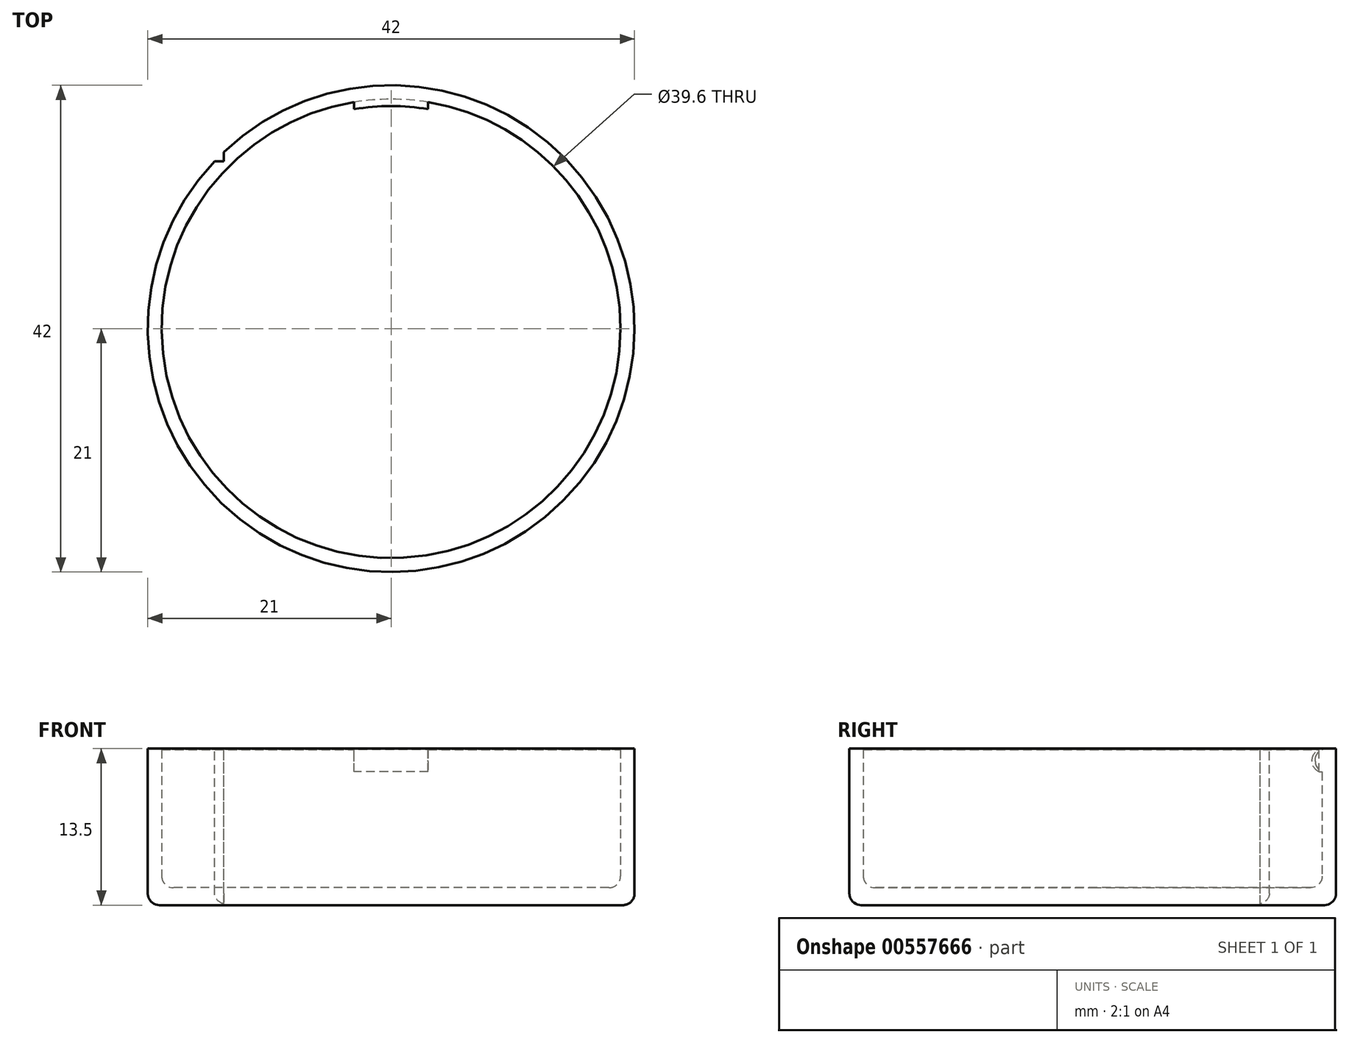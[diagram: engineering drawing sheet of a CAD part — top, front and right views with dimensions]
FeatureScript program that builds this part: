
annotation { "Feature Type Name" : "Feature", "Feature Type Description" : "" }
export const myFeature = defineFeature(function(context is Context, id is Id, definition is map)
    precondition{}
    {
        {
            var Q0;
            Q0=qCreatedBy(makeId("Top.planeOp"),FACE);
            var sketch = newSketch(context, id + "F0", { "sketchPlane" : qUnion([Q0])});
            skCircle(sketch, "E0", {"center": v(0, 0) * mm, "radius": 21 * mm});
            skSolve(sketch);
        }
        {
            var Q0;
            Q0=makeQuery(id+"F0.imprint","IMPRINT",FACE,{"disambiguationData":[TD([[makeQuery(id+"F0.imprint","IMPRINT",EDGE,{"derivedFrom":sQuery(id+"F0.wireOp",EDGE,"E0")}),1.0]])]});
            extrude(context, id + "F1", {"entities" : qUnion([Q0]), "depth" : 1.5 * mm, "offsetDistance" : 25 * mm});
        }
        {
            var Q0;
            Q0=makeQuery(id+"F1.opExtrude","CAP_FACE",FACE,{"disambiguationData":[OSD([sQuery(id+"F0.wireOp",EDGE,"E0")])],"isStart":false});
            var sketch = newSketch(context, id + "F2", { "sketchPlane" : qUnion([Q0])});
            skCircle(sketch, "E1", {"center": v(0, 0) * mm, "radius": 19.8 * mm});
            skCircle(sketch, "E2", {"center": v(0, 0) * mm, "radius": 21 * mm});
            skSolve(sketch);
        }
        {
            var Q0;
            Q0=makeQuery(id+"F2.imprint","IMPRINT",FACE,{"disambiguationData":[TD([[makeQuery(id+"F2.imprint","IMPRINT",EDGE,{"derivedFrom":sQuery(id+"F2.wireOp",EDGE,"E1")}),-1.0]])]});
            extrude(context, id + "F3", {"entities" : qUnion([Q0]), "operationType" : NewBodyOperationType.ADD, "depth" : 12 * mm, "offsetDistance" : 25 * mm});
        }
        {
            var Q0;
            Q0=makeQuery(id+"F1.opExtrude","CAP_EDGE",EDGE,{"disambiguationData":[OSD([sQuery(id+"F0.wireOp",EDGE,"E0")])],"isStart":true});
            fillet(context, id + "F4", {"entities" : qUnion([Q0]), "radius" : 1 * mm, "tangentPropagation" : true, "allowEdgeOverflow" : false});
        }
        {
            var Q0;
            Q0=makeQuery(id+"F3.opExtrude","CAP_FACE",FACE,{"disambiguationData":[OSD([sQuery(id+"F2.wireOp",EDGE,"E1"),sQuery(id+"F2.wireOp",EDGE,"E2")])],"isStart":false});
            var sketch = newSketch(context, id + "F5", { "sketchPlane" : qUnion([Q0])});
            skLineSegment(sketch, "E3", {"start": v(-15.24, 14.44) * mm, "end": v(-14.44, 14.44) * mm});
            skLineSegment(sketch, "E4", {"start": v(-14.44, 14.44) * mm, "end": v(-14.44, 15.24) * mm});
            skArc(sketch, "E5", {"start": v(-14.44, 15.24) * mm, "mid": v(-14.85, 14.85) * mm, "end": v(-15.24, 14.44) * mm});
            skSolve(sketch);
        }
        {
            var Q0;
            Q0=makeQuery(id+"F5.imprint","IMPRINT",FACE,{"disambiguationData":[TD([[makeQuery(id+"F5.imprint","IMPRINT",EDGE,{"derivedFrom":sQuery(id+"F5.wireOp",EDGE,"E3")}),1.0]])]});
            extrude(context, id + "F6", {"entities" : qUnion([Q0]), "operationType" : NewBodyOperationType.REMOVE, "oppositeDirection" : true, "depth" : 25 * mm, "offsetDistance" : 25 * mm});
        }
        {
            var Q0;
            Q0=makeQuery(id+"F1.opExtrude","CAP_FACE",FACE,{"disambiguationData":[OSD([sQuery(id+"F0.wireOp",EDGE,"E0")])],"isStart":false});
            var Q1;
            Q1=makeQuery(id+"F6.boolean.opBoolean","COPY",EDGE,{"derivedFrom":makeQuery(id+"F6.opExtrude","SWEPT_EDGE",EDGE,{"disambiguationData":[OSD([sQuery(id+"F2.wireOp",EDGE,"E2"),sQuery(id+"F5.wireOp",EDGE,"E4"),sQuery(id+"F5.wireOp",EDGE,"E5")])]})});
            var Q2;
            Q2=makeQuery(id+"F6.boolean.opBoolean","COPY",EDGE,{"derivedFrom":makeQuery(id+"F6.opExtrude","SWEPT_EDGE",EDGE,{"disambiguationData":[OSD([sQuery(id+"F2.wireOp",EDGE,"E2"),sQuery(id+"F5.wireOp",EDGE,"E3"),sQuery(id+"F5.wireOp",EDGE,"E5")])]})});
            fillet(context, id + "F7", {"entities" : qUnion([Q0, Q1, Q2]), "radius" : 1 * mm, "tangentPropagation" : true, "allowEdgeOverflow" : false});
        }
        {
            var Q0;
            Q0=makeQuery(id+"F3.opExtrude","CAP_FACE",FACE,{"disambiguationData":[OSD([sQuery(id+"F2.wireOp",EDGE,"E1"),sQuery(id+"F2.wireOp",EDGE,"E2")])],"isStart":false});
            var sketch = newSketch(context, id + "F8", { "sketchPlane" : qUnion([Q0])});
            skLineSegment(sketch, "E6", {"start": v(-3.2, 19.54) * mm, "end": v(-3.2, 18.93) * mm});
            skArc(sketch, "E7", {"start": v(3.2, 18.93) * mm, "mid": v(0, 19.2) * mm, "end": v(-3.2, 18.93) * mm});
            skLineSegment(sketch, "E8", {"start": v(3.2, 18.93) * mm, "end": v(3.2, 19.54) * mm});
            skArc(sketch, "E9", {"start": v(3.2, 19.54) * mm, "mid": v(0, 19.8) * mm, "end": v(-3.2, 19.54) * mm});
            skSolve(sketch);
        }
        {
            var Q0;
            Q0=makeQuery(id+"F8.imprint","IMPRINT",FACE,{"disambiguationData":[TD([[makeQuery(id+"F8.imprint","IMPRINT",EDGE,{"derivedFrom":sQuery(id+"F8.wireOp",EDGE,"E6")}),1.0]])]});
            extrude(context, id + "F9", {"entities" : qUnion([Q0]), "operationType" : NewBodyOperationType.ADD, "oppositeDirection" : true, "depth" : 2 * mm, "offsetDistance" : 25 * mm});
        }
        {
            var Q0;
            Q0=makeQuery(id+"F9.opExtrude","CAP_EDGE",EDGE,{"disambiguationData":[OSD([sQuery(id+"F8.wireOp",EDGE,"E7")])],"isStart":true});
            var Q1;
            Q1=makeQuery(id+"F9.opExtrude","CAP_EDGE",EDGE,{"disambiguationData":[OSD([sQuery(id+"F8.wireOp",EDGE,"E7")])],"isStart":false});
            fillet(context, id + "F10", {"entities" : qUnion([Q0, Q1]), "radius" : 1 * mm, "tangentPropagation" : true, "allowEdgeOverflow" : false});
        }
    });
